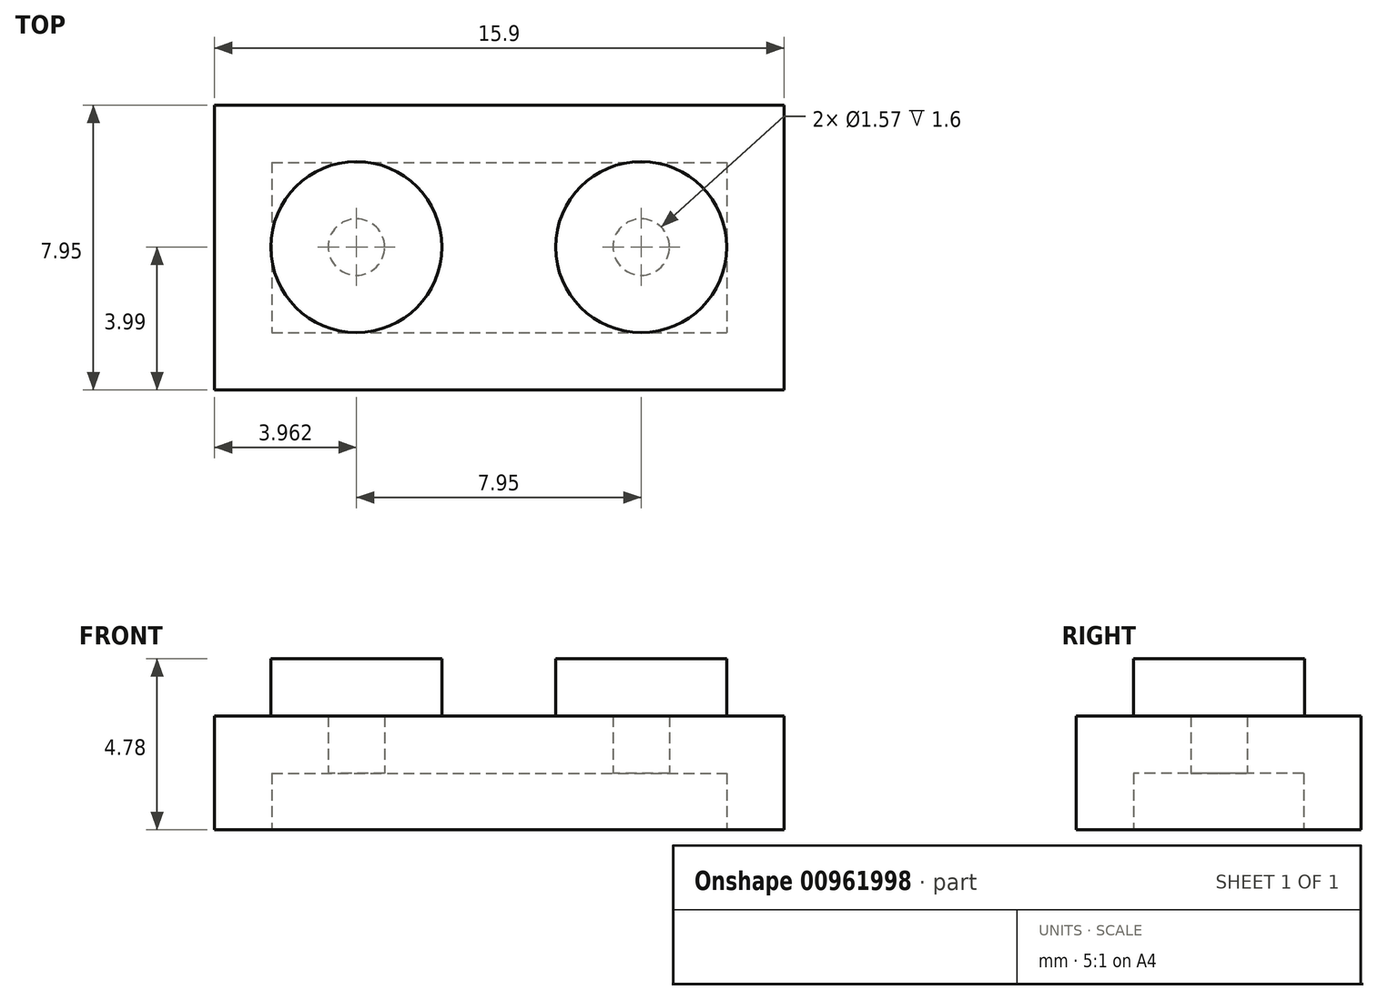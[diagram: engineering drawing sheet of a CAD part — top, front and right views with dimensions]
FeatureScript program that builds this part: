
annotation { "Feature Type Name" : "Feature", "Feature Type Description" : "" }
export const myFeature = defineFeature(function(context is Context, id is Id, definition is map)
    precondition{}
    {
        {
            var Q0;
            Q0=qCreatedBy(makeId("Top.planeOp"),FACE);
            var sketch = newSketch(context, id + "F0", { "sketchPlane" : qUnion([Q0])});
            skLineSegment(sketch, "E0.bottom", {"start": v(-15.9, 22.18) * mm, "end": v(0, 22.18) * mm});
            skLineSegment(sketch, "E0.top", {"start": v(-15.9, 14.23) * mm, "end": v(0, 14.23) * mm});
            skLineSegment(sketch, "E0.left", {"start": v(-15.9, 22.18) * mm, "end": v(-15.9, 14.23) * mm});
            skLineSegment(sketch, "E0.right", {"start": v(0, 22.18) * mm, "end": v(0, 14.23) * mm});
            skCircle(sketch, "E1", {"center": v(-11.94, 18.22) * mm, "radius": 2.39 * mm});
            skCircle(sketch, "E2.1.0.0", {"center": v(-3.99, 18.22) * mm, "radius": 2.39 * mm});
            skLineSegment(sketch, "E2.direction1", {"start": v(-11.94, 18.22) * mm, "end": v(-3.99, 18.22) * mm, "construction": true});
            skSolve(sketch);
        }
        {
            var Q0;
            Q0=makeQuery(id+"F0.imprint","IMPRINT",FACE,{"disambiguationData":[TD([[makeQuery(id+"F0.imprint","IMPRINT",EDGE,{"derivedFrom":sQuery(id+"F0.wireOp",EDGE,"E0.bottom")}),-1.0]])]});
            extrude(context, id + "F1", {"entities" : qUnion([Q0]), "depth" : 3.17 * mm, "offsetDistance" : 25.4 * mm});
        }
        {
            var Q0;
            Q0=makeQuery(id+"F0.imprint","IMPRINT",FACE,{"disambiguationData":[TD([[makeQuery(id+"F0.imprint","IMPRINT",EDGE,{"derivedFrom":sQuery(id+"F0.wireOp",EDGE,"E1")}),1.0]])]});
            var Q1;
            Q1=makeQuery(id+"F0.imprint","IMPRINT",FACE,{"disambiguationData":[TD([[makeQuery(id+"F0.imprint","IMPRINT",EDGE,{"derivedFrom":sQuery(id+"F0.wireOp",EDGE,"E2.1.0.0")}),1.0]])]});
            extrude(context, id + "F2", {"entities" : qUnion([Q0, Q1]), "operationType" : NewBodyOperationType.ADD, "depth" : 4.78 * mm, "offsetDistance" : 25.4 * mm});
        }
        {
            var Q0;
            {var subQ0=sQuery(id+"F0.wireOp",EDGE,"E2.1.0.0");var subQ1=sQuery(id+"F0.wireOp",EDGE,"E1");Q0=makeQuery(id+"F2.boolean.opBoolean","MERGE",FACE,{"derivedFrom":[makeQuery(id+"F1.opExtrude","CAP_FACE",FACE,{"disambiguationData":[OSD([sQuery(id+"F0.wireOp",EDGE,"E0.bottom"),sQuery(id+"F0.wireOp",EDGE,"E0.top"),sQuery(id+"F0.wireOp",EDGE,"E0.left"),sQuery(id+"F0.wireOp",EDGE,"E0.right"),subQ1,subQ0])],"isStart":true}),makeQuery(id+"F2.opExtrude","CAP_FACE",FACE,{"disambiguationData":[OSD([subQ1])],"isStart":true}),makeQuery(id+"F2.opExtrude","CAP_FACE",FACE,{"disambiguationData":[OSD([subQ0])],"isStart":true})]});}
            shell(context, id + "F3", {"entities" : qUnion([Q0]), "thickness" : 1.6 * mm});
        }
    });
